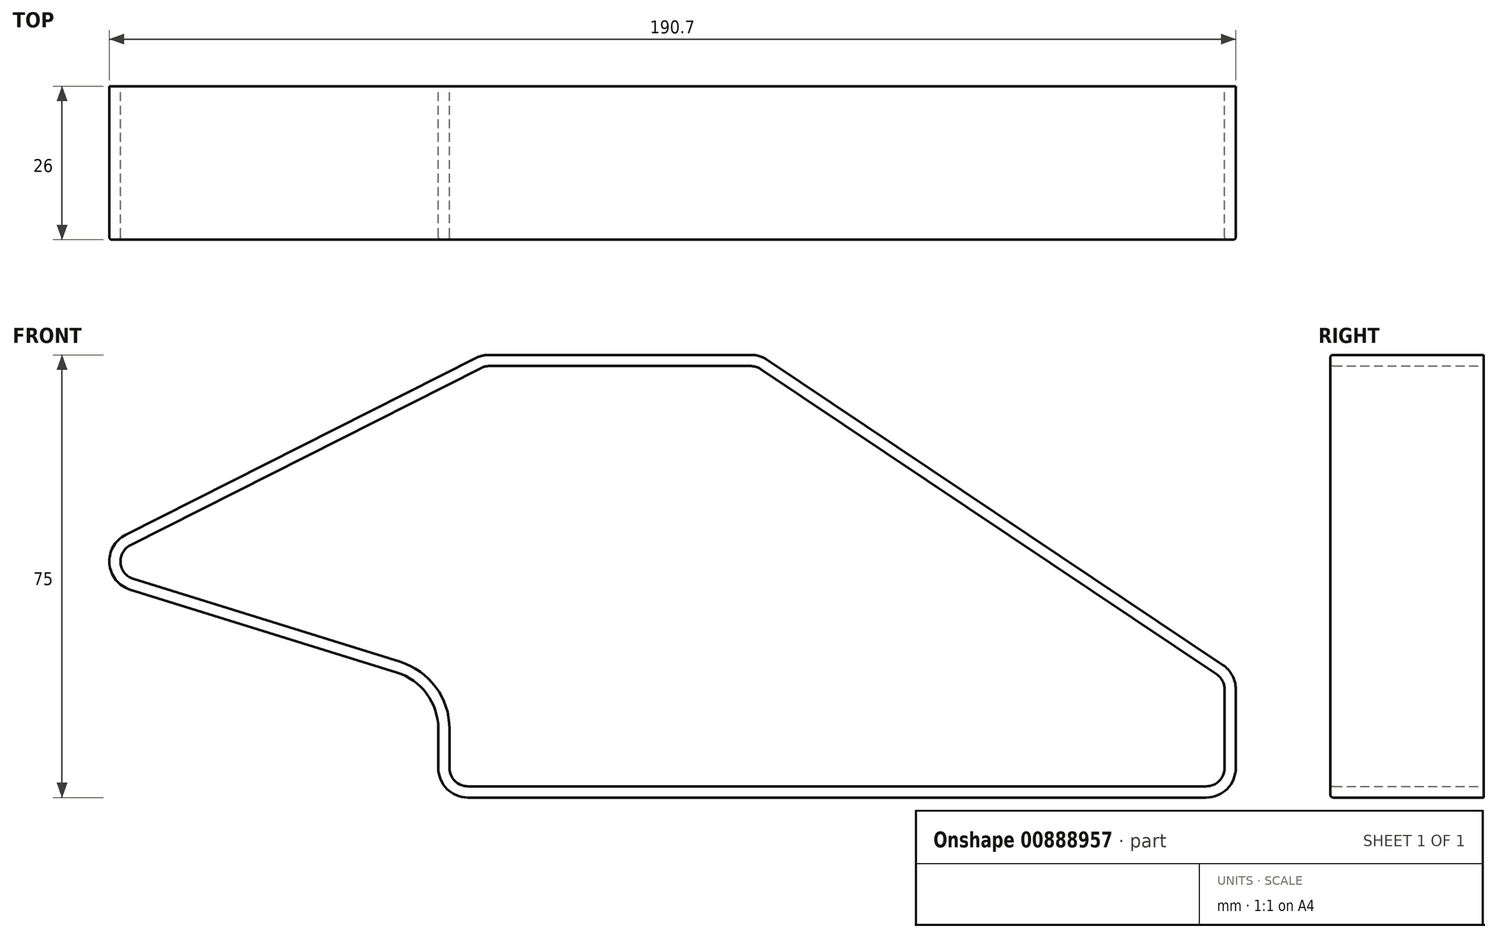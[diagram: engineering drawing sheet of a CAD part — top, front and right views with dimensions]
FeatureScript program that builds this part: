
annotation { "Feature Type Name" : "Feature", "Feature Type Description" : "" }
export const myFeature = defineFeature(function(context is Context, id is Id, definition is map)
    precondition{}
    {
        {
            var Q0;
            Q0=qCreatedBy(makeId("Front.planeOp"),FACE);
            var sketch = newSketch(context, id + "F0", { "sketchPlane" : qUnion([Q0])});
            skLineSegment(sketch, "E0", {"start": v(0, -7.36) * mm, "end": v(0, -14) * mm});
            skLineSegment(sketch, "E1", {"start": v(5, -19) * mm, "end": v(130, -19) * mm});
            skLineSegment(sketch, "E2", {"start": v(135, -14) * mm, "end": v(135, -0.67) * mm});
            skLineSegment(sketch, "E3", {"start": v(132.78, 3.49) * mm, "end": v(55.68, 55.15) * mm});
            skLineSegment(sketch, "E4", {"start": v(52.9, 56) * mm, "end": v(8.61, 56) * mm});
            skLineSegment(sketch, "E5", {"start": v(6.36, 55.46) * mm, "end": v(-52.96, 25.48) * mm});
            skLineSegment(sketch, "E6", {"start": v(-52.19, 16.24) * mm, "end": v(-7.03, 2.19) * mm});
            skPoint(sketch, "E7.visualSharp", {"position": v(-63.97, 19.9) * mm});
            skArc(sketch, "E7.filletArc", {"start": v(-52.96, 25.48) * mm, "mid": v(-55.69, 20.6) * mm, "end": v(-52.19, 16.24) * mm});
            skPoint(sketch, "E8.visualSharp", {"position": v(7.42, 56) * mm});
            skArc(sketch, "E8.filletArc", {"start": v(8.61, 56) * mm, "mid": v(7.45, 55.86) * mm, "end": v(6.36, 55.46) * mm});
            skPoint(sketch, "E9.visualSharp", {"position": v(54.42, 56) * mm});
            skArc(sketch, "E9.filletArc", {"start": v(55.68, 55.15) * mm, "mid": v(54.36, 55.78) * mm, "end": v(52.9, 56) * mm});
            skPoint(sketch, "E10.visualSharp", {"position": v(135, 2) * mm});
            skArc(sketch, "E10.filletArc", {"start": v(135, -0.67) * mm, "mid": v(134.41, 1.69) * mm, "end": v(132.78, 3.49) * mm});
            skPoint(sketch, "E11.visualSharp", {"position": v(135, -19) * mm});
            skArc(sketch, "E11.filletArc", {"start": v(130, -19) * mm, "mid": v(133.54, -17.54) * mm, "end": v(135, -14) * mm});
            skPoint(sketch, "E12.visualSharp", {"position": v(0, -19) * mm});
            skArc(sketch, "E12.filletArc", {"start": v(0, -14) * mm, "mid": v(1.46, -17.54) * mm, "end": v(5, -19) * mm});
            skPoint(sketch, "E13.visualSharp", {"position": v(0, 0) * mm});
            skArc(sketch, "E13.filletArc", {"start": v(0, -7.36) * mm, "mid": v(-1.95, -1.43) * mm, "end": v(-7.03, 2.19) * mm});
            skLineSegment(sketch, "E14.0", {"start": v(7.21, 53.77) * mm, "end": v(-52.1, 23.78) * mm});
            skArc(sketch, "E14.1", {"start": v(8.61, 54.1) * mm, "mid": v(7.9, 54.02) * mm, "end": v(7.21, 53.77) * mm});
            skLineSegment(sketch, "E14.2", {"start": v(52.9, 54.1) * mm, "end": v(8.61, 54.1) * mm});
            skArc(sketch, "E14.3", {"start": v(1.9, -14) * mm, "mid": v(2.8, -16.2) * mm, "end": v(5, -17.1) * mm});
            skLineSegment(sketch, "E14.4", {"start": v(1.9, -7.36) * mm, "end": v(1.9, -14) * mm});
            skArc(sketch, "E14.5", {"start": v(1.9, -7.36) * mm, "mid": v(-0.42, -0.3) * mm, "end": v(-6.46, 4) * mm});
            skLineSegment(sketch, "E14.6", {"start": v(-51.62, 18.05) * mm, "end": v(-6.46, 4) * mm});
            skLineSegment(sketch, "E14.7", {"start": v(5, -17.1) * mm, "end": v(130, -17.1) * mm});
            skArc(sketch, "E14.8", {"start": v(130, -17.1) * mm, "mid": v(132.2, -16.2) * mm, "end": v(133.1, -14) * mm});
            skLineSegment(sketch, "E14.9", {"start": v(133.1, -14) * mm, "end": v(133.1, -0.67) * mm});
            skArc(sketch, "E14.10", {"start": v(-52.1, 23.78) * mm, "mid": v(-53.8, 20.76) * mm, "end": v(-51.62, 18.05) * mm});
            skArc(sketch, "E14.11", {"start": v(133.1, -0.67) * mm, "mid": v(132.73, 0.8) * mm, "end": v(131.73, 1.9) * mm});
            skLineSegment(sketch, "E14.12", {"start": v(131.73, 1.9) * mm, "end": v(54.63, 53.58) * mm});
            skArc(sketch, "E14.13", {"start": v(54.63, 53.58) * mm, "mid": v(53.8, 53.97) * mm, "end": v(52.9, 54.1) * mm});
            skSolve(sketch);
        }
        {
            var Q0;
            Q0=makeQuery(id+"F0.imprint","IMPRINT",FACE,{"disambiguationData":[TD([[makeQuery(id+"F0.imprint","IMPRINT",EDGE,{"derivedFrom":sQuery(id+"F0.wireOp",EDGE,"E0")}),1.0]])]});
            extrude(context, id + "F1", {"entities" : qUnion([Q0]), "depth" : 26 * mm, "offsetDistance" : 25 * mm});
        }
        {
            var Q0;
            Q0=makeQuery(id+"F1.opExtrude","CAP_EDGE",EDGE,{"disambiguationData":[OSD([sQuery(id+"F0.wireOp",EDGE,"E1")])],"isStart":false});
            var Q1;
            Q1=makeQuery(id+"F1.opExtrude","CAP_EDGE",EDGE,{"disambiguationData":[OSD([sQuery(id+"F0.wireOp",EDGE,"E14.7")])],"isStart":false});
            fillet(context, id + "F2", {"entities" : qUnion([Q0, Q1]), "radius" : .5 * mm, "tangentPropagation" : true, "allowEdgeOverflow" : false});
        }
    });
